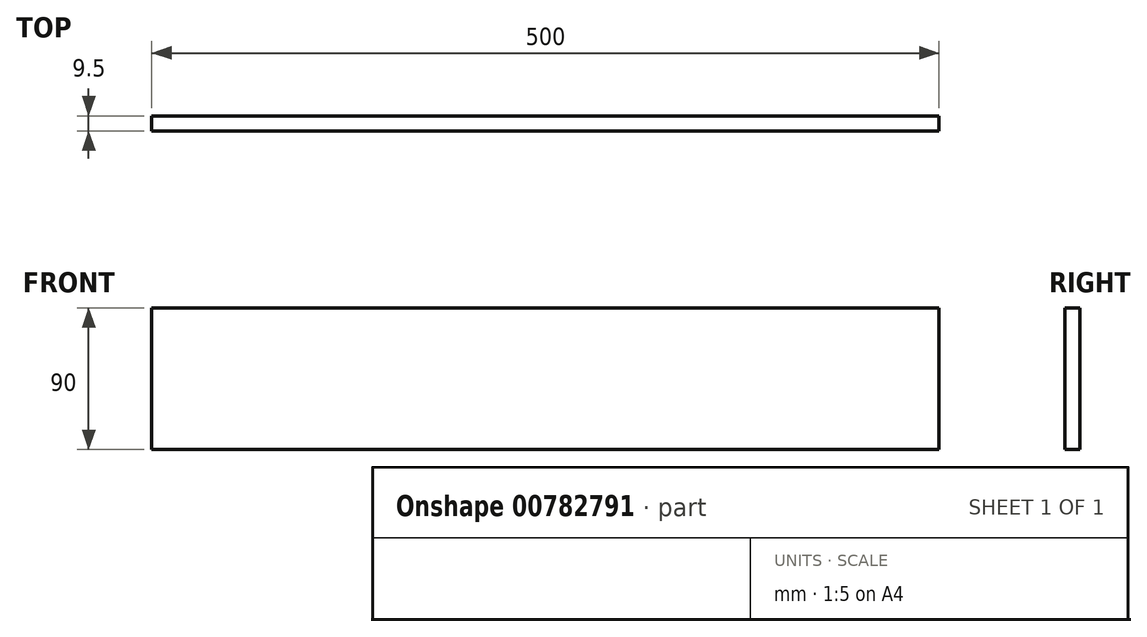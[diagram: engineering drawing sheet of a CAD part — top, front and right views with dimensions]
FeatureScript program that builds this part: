
annotation { "Feature Type Name" : "Feature", "Feature Type Description" : "" }
export const myFeature = defineFeature(function(context is Context, id is Id, definition is map)
    precondition{}
    {
        {
            var Q0;
            Q0=qCreatedBy(makeId("Front.planeOp"),FACE);
            var sketch = newSketch(context, id + "F0", { "sketchPlane" : qUnion([Q0])});
            skLineSegment(sketch, "E0.bottom", {"start": v(-40.88, 110.2) * mm, "end": v(459.12, 110.2) * mm});
            skLineSegment(sketch, "E0.top", {"start": v(-40.88, 20.2) * mm, "end": v(459.12, 20.2) * mm});
            skLineSegment(sketch, "E0.left", {"start": v(-40.88, 110.2) * mm, "end": v(-40.88, 20.2) * mm});
            skLineSegment(sketch, "E0.right", {"start": v(459.12, 110.2) * mm, "end": v(459.12, 20.2) * mm});
            skSolve(sketch);
        }
        {
            var Q0;
            Q0 = qSketchRegion(id + "F0", true);
            extrude(context, id + "F1", {"entities" : qUnion([Q0]), "depth" : 9.5 * mm, "offsetDistance" : 25 * mm});
        }
    });
